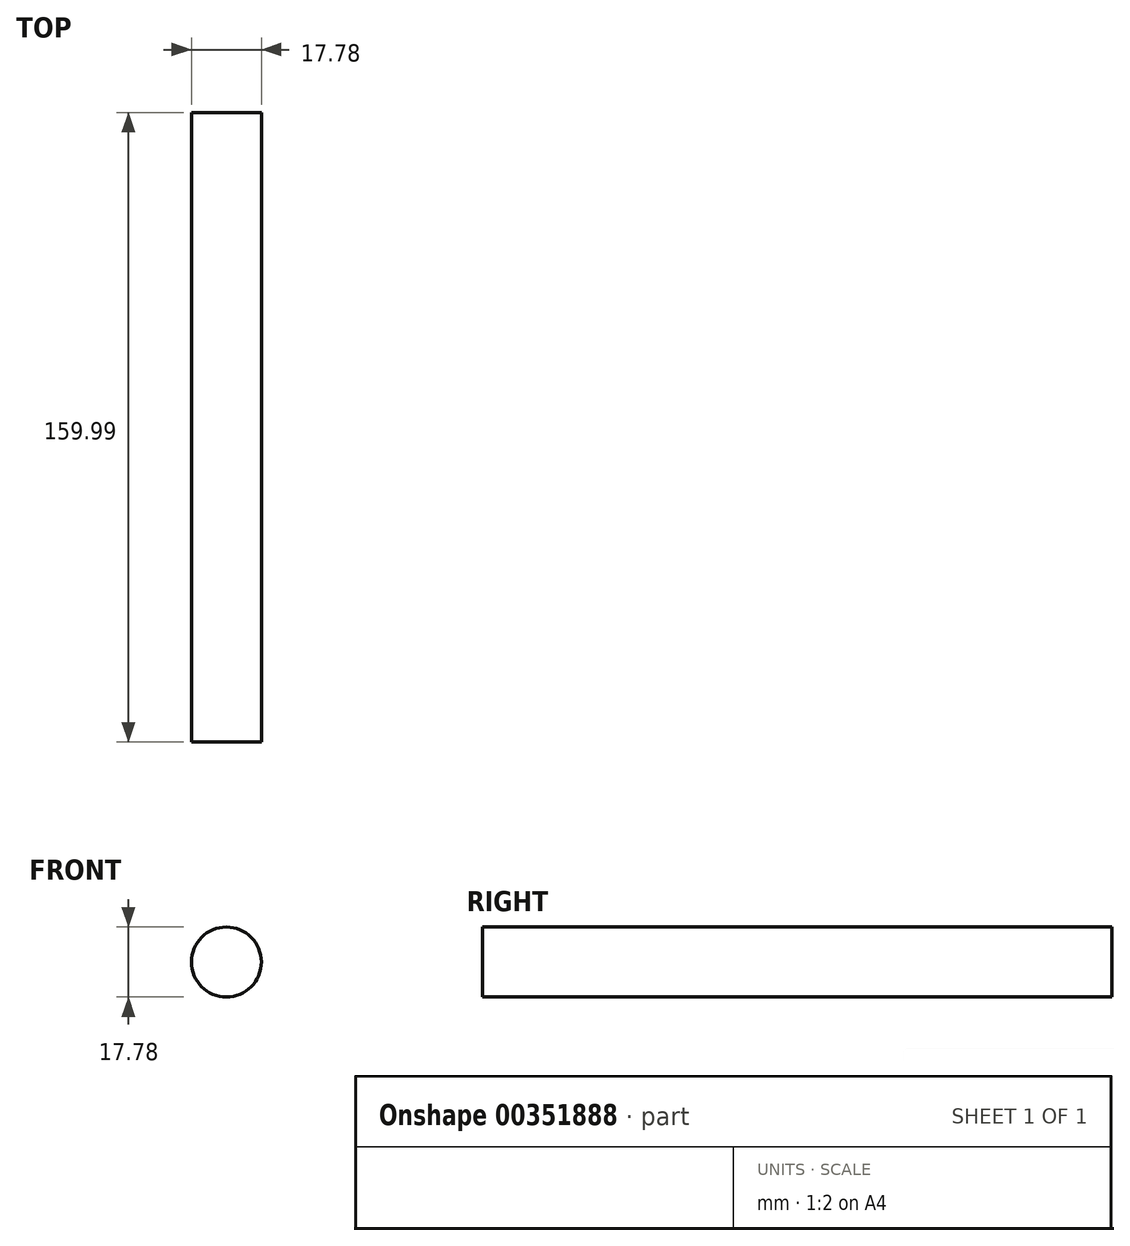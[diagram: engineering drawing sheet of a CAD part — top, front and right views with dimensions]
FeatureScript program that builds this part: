
annotation { "Feature Type Name" : "Feature", "Feature Type Description" : "" }
export const myFeature = defineFeature(function(context is Context, id is Id, definition is map)
    precondition{}
    {
        {
            var Q0;
            Q0=qCreatedBy(makeId("Front.planeOp"),FACE);
            var sketch = newSketch(context, id + "F0", { "sketchPlane" : qUnion([Q0])});
            skCircle(sketch, "E0", {"center": v(0, 0) * mm, "radius": 8.9 * mm});
            skSolve(sketch);
        }
        {
            var Q0;
            Q0 = qSketchRegion(id + "F0", true);
            extrude(context, id + "F1", {"entities" : qUnion([Q0]), "depth" : 160 * mm});
        }
    });
